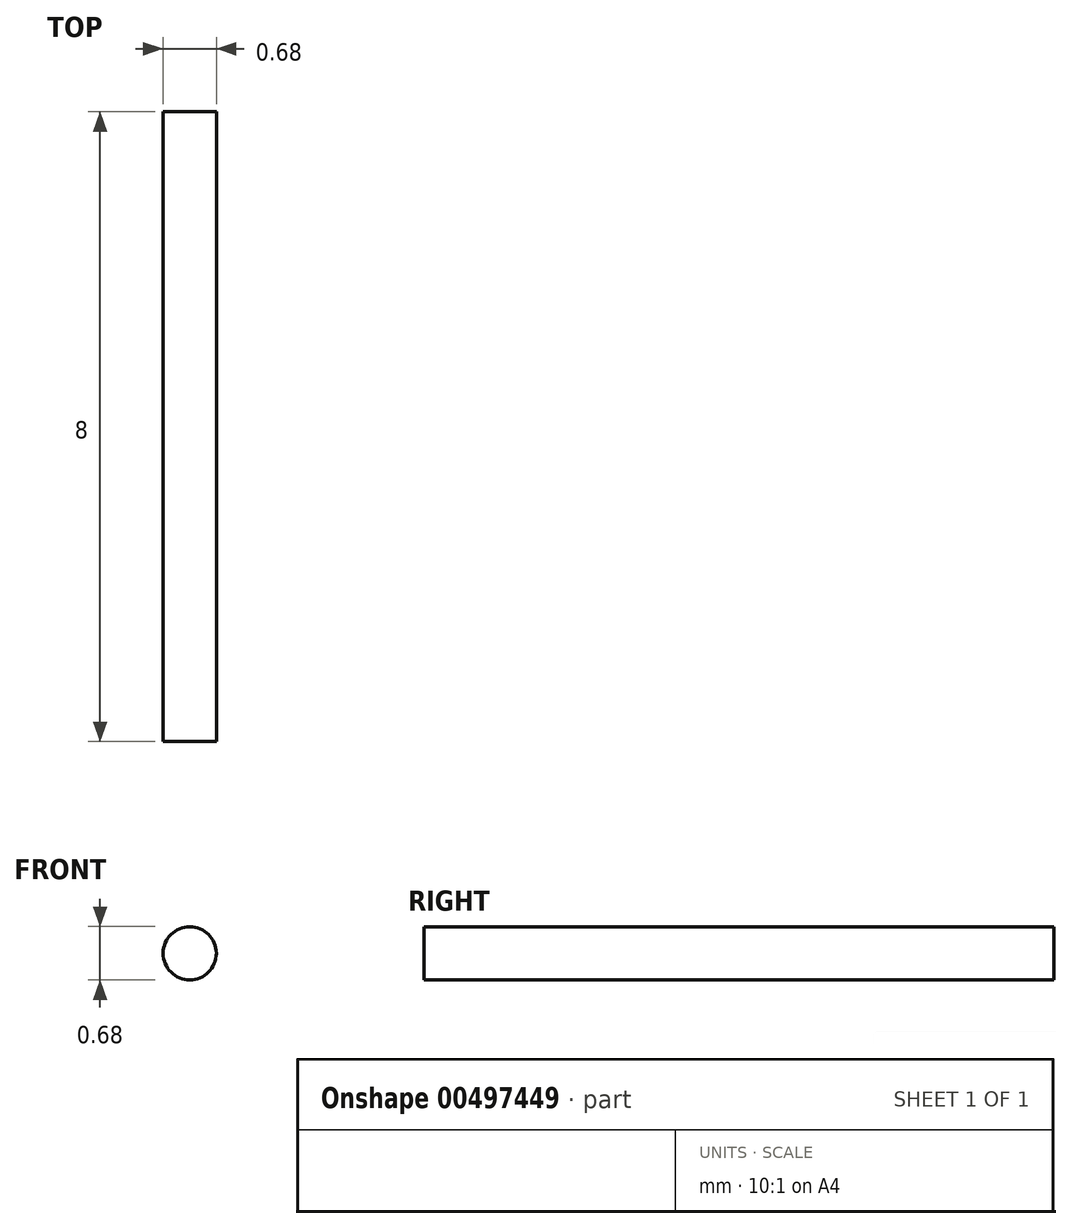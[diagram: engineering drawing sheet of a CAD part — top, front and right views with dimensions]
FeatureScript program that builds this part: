
annotation { "Feature Type Name" : "Feature", "Feature Type Description" : "" }
export const myFeature = defineFeature(function(context is Context, id is Id, definition is map)
    precondition{}
    {
        {
            var Q0;
            Q0=qCreatedBy(makeId("Front.planeOp"),FACE);
            var sketch = newSketch(context, id + "F0", { "sketchPlane" : qUnion([Q0])});
            skCircle(sketch, "E0", {"center": v(0, 0) * mm, "radius": 0.34 * mm});
            skSolve(sketch);
        }
        {
            var Q0;
            Q0=qSketchRegion(id+"F0",true);
            extrude(context, id + "F1", {"entities" : qUnion([Q0]), "depth" : 8 * mm});
        }
    });
